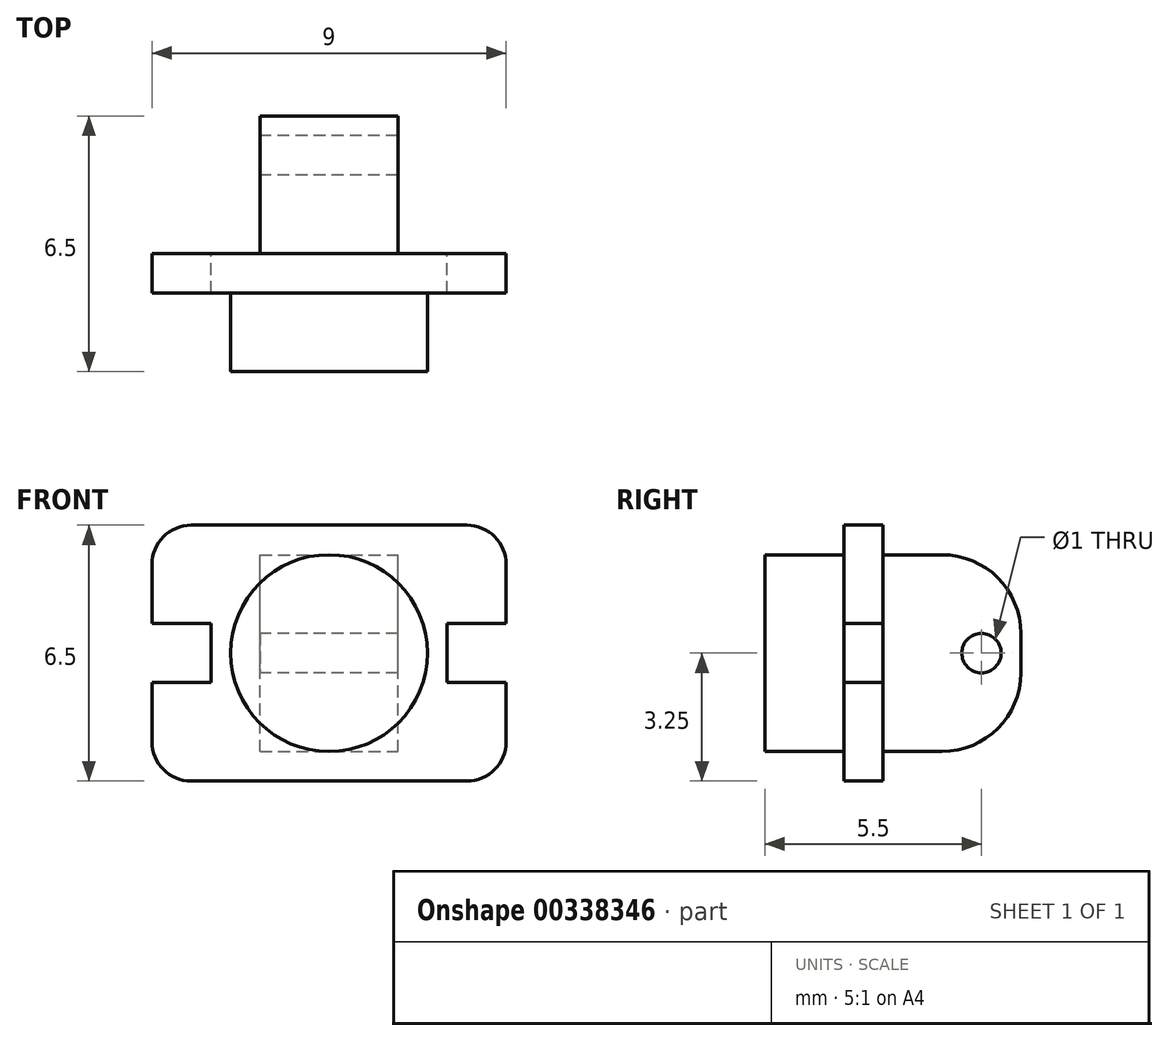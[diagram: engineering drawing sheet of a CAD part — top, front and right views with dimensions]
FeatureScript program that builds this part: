
annotation { "Feature Type Name" : "Feature", "Feature Type Description" : "" }
export const myFeature = defineFeature(function(context is Context, id is Id, definition is map)
    precondition{}
    {
        {
            var Q0;
            Q0=qCreatedBy(makeId("Front.planeOp"),FACE);
            var sketch = newSketch(context, id + "F0", { "sketchPlane" : qUnion([Q0])});
            skCircle(sketch, "E0", {"center": v(0, 0) * mm, "radius": 2.5 * mm});
            skSolve(sketch);
        }
        {
            var Q0;
            Q0=makeQuery(id+"F0.imprint","IMPRINT",FACE,{"disambiguationData":[TD([[makeQuery(id+"F0.imprint","IMPRINT",EDGE,{"derivedFrom":sQuery(id+"F0.wireOp",EDGE,"E0")}),1.0]])]});
            extrude(context, id + "F1", {"entities" : qUnion([Q0]), "depth" : 2 * mm});
        }
        {
            var Q0;
            Q0=qCreatedBy(makeId("Front.planeOp"),FACE);
            var sketch = newSketch(context, id + "F2", { "sketchPlane" : qUnion([Q0])});
            skLineSegment(sketch, "E1.bottom", {"start": v(-4.5, -3.25) * mm, "end": v(4.5, -3.25) * mm});
            skLineSegment(sketch, "E1.top", {"start": v(-4.5, 3.25) * mm, "end": v(4.5, 3.25) * mm});
            skLineSegment(sketch, "E1.left", {"start": v(-4.5, -3.25) * mm, "end": v(-4.5, 3.25) * mm});
            skLineSegment(sketch, "E1.right", {"start": v(4.5, -3.25) * mm, "end": v(4.5, 3.25) * mm});
            skPoint(sketch, "E1.middle", {"position": v(0, 0) * mm});
            skSolve(sketch);
        }
        {
            var Q0;
            Q0=makeQuery(id+"F2.imprint","IMPRINT",FACE,{"disambiguationData":[TD([[makeQuery(id+"F2.imprint","IMPRINT",EDGE,{"derivedFrom":sQuery(id+"F2.wireOp",EDGE,"E1.bottom")}),1.0]])]});
            extrude(context, id + "F3", {"entities" : qUnion([Q0]), "operationType" : NewBodyOperationType.ADD, "oppositeDirection" : true, "depth" : 1 * mm});
        }
        {
            var Q0;
            Q0=makeQuery(id+"F3.opExtrude","CAP_FACE",FACE,{"disambiguationData":[OSD([sQuery(id+"F2.wireOp",EDGE,"E1.bottom"),sQuery(id+"F2.wireOp",EDGE,"E1.top"),sQuery(id+"F2.wireOp",EDGE,"E1.left"),sQuery(id+"F2.wireOp",EDGE,"E1.right")])],"isStart":false});
            var sketch = newSketch(context, id + "F4", { "sketchPlane" : qUnion([Q0])});
            skLineSegment(sketch, "E2.bottom", {"start": v(1.75, -2.5) * mm, "end": v(-1.75, -2.5) * mm});
            skLineSegment(sketch, "E2.top", {"start": v(1.75, 2.5) * mm, "end": v(-1.75, 2.5) * mm});
            skLineSegment(sketch, "E2.left", {"start": v(1.75, -2.5) * mm, "end": v(1.75, 2.5) * mm});
            skLineSegment(sketch, "E2.right", {"start": v(-1.75, -2.5) * mm, "end": v(-1.75, 2.5) * mm});
            skPoint(sketch, "E2.middle", {"position": v(0, 0) * mm});
            skSolve(sketch);
        }
        {
            var Q0;
            Q0=makeQuery(id+"F4.imprint","IMPRINT",FACE,{"disambiguationData":[TD([[makeQuery(id+"F4.imprint","IMPRINT",EDGE,{"derivedFrom":sQuery(id+"F4.wireOp",EDGE,"E2.bottom")}),-1.0]])]});
            extrude(context, id + "F5", {"entities" : qUnion([Q0]), "operationType" : NewBodyOperationType.ADD, "depth" : 3.5 * mm});
        }
        {
            var Q0;
            Q0=makeQuery(id+"F5.opExtrude","SWEPT_FACE",FACE,{"disambiguationData":[OSD([sQuery(id+"F4.wireOp",EDGE,"E2.left")])]});
            var sketch = newSketch(context, id + "F6", { "sketchPlane" : qUnion([Q0])});
            skCircle(sketch, "E3", {"center": v(-3.5, 0) * mm, "radius": 0.5 * mm});
            skSolve(sketch);
        }
        {
            var Q0;
            Q0=makeQuery(id+"F6.imprint","IMPRINT",FACE,{"disambiguationData":[TD([[makeQuery(id+"F6.imprint","IMPRINT",EDGE,{"derivedFrom":sQuery(id+"F6.wireOp",EDGE,"E3")}),1.0]])]});
            extrude(context, id + "F7", {"entities" : qUnion([Q0]), "operationType" : NewBodyOperationType.REMOVE, "oppositeDirection" : true, "depth" : 25 * mm});
        }
        {
            var Q0;
            Q0=makeQuery(id+"F5.opExtrude","CAP_EDGE",EDGE,{"disambiguationData":[OSD([sQuery(id+"F4.wireOp",EDGE,"E2.bottom")])],"isStart":false});
            var Q1;
            Q1=makeQuery(id+"F5.opExtrude","CAP_EDGE",EDGE,{"disambiguationData":[OSD([sQuery(id+"F4.wireOp",EDGE,"E2.top")])],"isStart":false});
            fillet(context, id + "F8", {"entities" : qUnion([Q0, Q1]), "radius" : 2 * mm, "tangentPropagation" : true, "allowEdgeOverflow" : false});
        }
        {
            var Q0;
            Q0=makeQuery(id+"F3.opExtrude","SWEPT_FACE",FACE,{"disambiguationData":[OSD([sQuery(id+"F2.wireOp",EDGE,"E1.left")])]});
            var sketch = newSketch(context, id + "F9", { "sketchPlane" : qUnion([Q0])});
            skLineSegment(sketch, "E4.bottom", {"start": v(0, -0.75) * mm, "end": v(-1, -0.75) * mm});
            skLineSegment(sketch, "E4.top", {"start": v(0, 0.75) * mm, "end": v(-1, 0.75) * mm});
            skLineSegment(sketch, "E4.left", {"start": v(0, -0.75) * mm, "end": v(0, 0.75) * mm});
            skLineSegment(sketch, "E4.right", {"start": v(-1, -0.75) * mm, "end": v(-1, 0.75) * mm});
            skPoint(sketch, "E4.middle", {"position": v(-0.5, 0) * mm});
            skSolve(sketch);
        }
        {
            var Q0;
            Q0=makeQuery(id+"F9.imprint","IMPRINT",FACE,{"disambiguationData":[TD([[makeQuery(id+"F9.imprint","IMPRINT",EDGE,{"derivedFrom":sQuery(id+"F9.wireOp",EDGE,"E4.bottom")}),-1.0]])]});
            extrude(context, id + "F10", {"entities" : qUnion([Q0]), "operationType" : NewBodyOperationType.REMOVE, "oppositeDirection" : true, "depth" : 1 * mm});
        }
        {
            var Q0;
            Q0=makeQuery(id+"F3.opExtrude","SWEPT_FACE",FACE,{"disambiguationData":[OSD([sQuery(id+"F2.wireOp",EDGE,"E1.right")])]});
            var sketch = newSketch(context, id + "F11", { "sketchPlane" : qUnion([Q0])});
            skLineSegment(sketch, "E5.bottom", {"start": v(1, -0.75) * mm, "end": v(0, -0.75) * mm});
            skLineSegment(sketch, "E5.top", {"start": v(1, 0.75) * mm, "end": v(0, 0.75) * mm});
            skLineSegment(sketch, "E5.left", {"start": v(1, -0.75) * mm, "end": v(1, 0.75) * mm});
            skLineSegment(sketch, "E5.right", {"start": v(0, -0.75) * mm, "end": v(0, 0.75) * mm});
            skPoint(sketch, "E5.middle", {"position": v(0.5, 0) * mm});
            skSolve(sketch);
        }
        {
            var Q0;
            Q0 = qSketchRegion(id + "F11", true);
            extrude(context, id + "F12", {"entities" : qUnion([Q0]), "operationType" : NewBodyOperationType.REMOVE, "oppositeDirection" : true, "depth" : 1 * mm});
        }
        {
            var Q0;
            Q0=makeQuery(id+"F3.opExtrude","SWEPT_EDGE",EDGE,{"disambiguationData":[OSD([sQuery(id+"F2.wireOp",EDGE,"E1.top"),sQuery(id+"F2.wireOp",EDGE,"E1.right")])]});
            var Q1;
            Q1=makeQuery(id+"F3.opExtrude","SWEPT_EDGE",EDGE,{"disambiguationData":[OSD([sQuery(id+"F2.wireOp",EDGE,"E1.bottom"),sQuery(id+"F2.wireOp",EDGE,"E1.right")])]});
            var Q2;
            Q2=makeQuery(id+"F3.opExtrude","SWEPT_EDGE",EDGE,{"disambiguationData":[OSD([sQuery(id+"F2.wireOp",EDGE,"E1.bottom"),sQuery(id+"F2.wireOp",EDGE,"E1.left")])]});
            var Q3;
            Q3=makeQuery(id+"F3.opExtrude","SWEPT_EDGE",EDGE,{"disambiguationData":[OSD([sQuery(id+"F2.wireOp",EDGE,"E1.top"),sQuery(id+"F2.wireOp",EDGE,"E1.left")])]});
            fillet(context, id + "F13", {"entities" : qUnion([Q0, Q1, Q2, Q3]), "radius" : 1 * mm, "tangentPropagation" : true, "allowEdgeOverflow" : false});
        }
        {
            var Q0;
            Q0=makeQuery(id+"F3.opExtrude","CAP_FACE",FACE,{"disambiguationData":[OSD([sQuery(id+"F2.wireOp",EDGE,"E1.bottom"),sQuery(id+"F2.wireOp",EDGE,"E1.top"),sQuery(id+"F2.wireOp",EDGE,"E1.left"),sQuery(id+"F2.wireOp",EDGE,"E1.right")])],"isStart":false});
            var sketch = newSketch(context, id + "F14", { "sketchPlane" : qUnion([Q0])});
            skLineSegment(sketch, "E6.bottom", {"start": v(-3.5, 0.75) * mm, "end": v(-3, 0.75) * mm});
            skLineSegment(sketch, "E6.top", {"start": v(-3.5, -0.75) * mm, "end": v(-3, -0.75) * mm});
            skLineSegment(sketch, "E6.left", {"start": v(-3.5, 0.75) * mm, "end": v(-3.5, -0.75) * mm});
            skLineSegment(sketch, "E6.right", {"start": v(-3, 0.75) * mm, "end": v(-3, -0.75) * mm});
            skSolve(sketch);
        }
        {
            var Q0;
            Q0=makeQuery(id+"F14.imprint","IMPRINT",FACE,{"disambiguationData":[TD([[makeQuery(id+"F14.imprint","IMPRINT",EDGE,{"derivedFrom":sQuery(id+"F14.wireOp",EDGE,"E6.bottom")}),1.0]])]});
            var sketch = newSketch(context, id + "F15", { "sketchPlane" : qUnion([Q0])});
            skLineSegment(sketch, "E7.bottom", {"start": v(3, -0.75) * mm, "end": v(3.5, -0.75) * mm});
            skLineSegment(sketch, "E7.top", {"start": v(3, 0.75) * mm, "end": v(3.5, 0.75) * mm});
            skLineSegment(sketch, "E7.left", {"start": v(3, -0.75) * mm, "end": v(3, 0.75) * mm});
            skLineSegment(sketch, "E7.right", {"start": v(3.5, -0.75) * mm, "end": v(3.5, 0.75) * mm});
            skSolve(sketch);
        }
        {
            var Q0;
            Q0=makeQuery(id+"F15.imprint","IMPRINT",FACE,{"disambiguationData":[TD([[makeQuery(id+"F15.imprint","IMPRINT",EDGE,{"derivedFrom":sQuery(id+"F15.wireOp",EDGE,"E7.bottom")}),1.0]])]});
            var Q1;
            Q1=makeQuery(id+"F14.imprint","IMPRINT",FACE,{"disambiguationData":[TD([[makeQuery(id+"F14.imprint","IMPRINT",EDGE,{"derivedFrom":sQuery(id+"F14.wireOp",EDGE,"E6.bottom")}),-1.0]])]});
            extrude(context, id + "F16", {"entities" : qUnion([Q0, Q1]), "operationType" : NewBodyOperationType.REMOVE, "oppositeDirection" : true, "depth" : 25 * mm});
        }
    });
